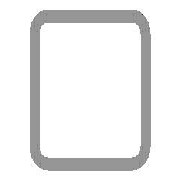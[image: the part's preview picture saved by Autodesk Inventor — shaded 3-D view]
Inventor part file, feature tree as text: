
AUTODESK INVENTOR PART (.ipt)
format: ipt  version: 2025.3 (Build 293356030, 356C)  size: 151,040 bytes
history: native  units: mm (DEFAULTED — no unit token found)
features: other x4, plane x3, split x2, sketch x1
ambient origin geometry x8: Origin, YZ Plane, XZ Plane, XY Plane, X Axis, Y Axis, Z Axis, Center Point
bodies: Solid1 (feature_tree), Body (feature_tree)
feature tree (10):
  parser-record x1  (decoder bookkeeping rows leaked as tree rows — omitted from the tree; the rows remain in map.json)
  other  "Driven Length"
  other  "Start plane"
  other  "End plane"
  plane  "Work Plane4"
  split  "Split1"
  plane  "Work Plane5"
  split  "Split2"
  sketch  "Sketch3"  dims[d3=839.332008mm d4=0.0mm d7=4.0mm d9=40.0mm d11=40.0mm d12=2.0mm d13=193.468323mm d14=1032.800331mm d15=20.0mm d16=20.0mm d17=90.0deg d18=839.332008mm]
  plane  "Work Plane3"
